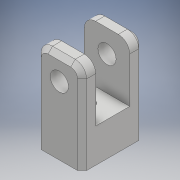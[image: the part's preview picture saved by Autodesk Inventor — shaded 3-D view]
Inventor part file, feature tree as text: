
AUTODESK INVENTOR PART (.ipt)
format: ipt  version: 2017 (Build 210142000, 142)  size: 153,088 bytes
history: native  units: mm
features: extrude x4, sketch x3, fillet x1, chamfer x1
ambient origin geometry x8: Origin, YZ Plane, XZ Plane, XY Plane, X Axis, Y Axis, Z Axis, Center Point
bodies: Solid1 (feature_tree)
feature tree (9):
  sketch  "Sketch1"  dims[d0=15.0mm d1=20.0mm]
  extrude  "Extrusion1"  Depth=20.0mm
  extrude  "Extrusion2"  Depth=15.0mm TaperAngle=0.0deg
  extrude  "Extrusion3"  Depth=25.0mm
  fillet  "Fillet1"  Radius=10.0mm
  extrude  "Extrusion4"  Depth=25.0mm TaperAngle=0.0deg
  chamfer  "Chamfer1"  Distance=5.0mm
  sketch  "Sketch2"  dims[d2=6.0mm d3=15.0mm d4=0.0mm]
  sketch  "Sketch3"  dims[d5=25.0mm d6=0.0mm d7=8.0mm d8=10.0mm d9=25.0mm d10=0.0mm d11=5.0mm d12=4.3mm d13=25.0mm d14=0.0mm d15=2.0mm d16=2.0mm d17=45.0deg]
